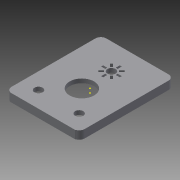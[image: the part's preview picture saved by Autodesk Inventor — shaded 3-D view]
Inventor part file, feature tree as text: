
AUTODESK INVENTOR PART (.ipt)
format: ipt  version: 2015 SP1 (Build 190203100, 203)  size: 220,160 bytes
history: native  units: mm
features: sketch x6, extrude x4, reference x4, other x2, projected_geometry x1
ambient origin geometry x8: Origin, YZ Plane, XZ Plane, XY Plane, X Axis, Y Axis, Z Axis, Center Point
bodies: Body1 (feature_tree)
feature tree (17):
  other  "Sólido1"
  sketch  "Boceto1"  dims[d0=1.5mm d1=0.0mm]
  extrude  "Extrusión1"  Depth=1.0mm
  sketch  "Boceto3"  dims[d9=9.0mm d10=1.5mm d11=0.0mm]
  other  "Labio1"
  extrude  "Extrusión2"  Depth=1.5mm TaperAngle=0.0deg
  sketch  "Boceto7"  dims[d40=1.5mm d41=80.0mm d43=360.0deg]
  extrude  "Extrusión4"  Depth=10.0mm TaperAngle=0.0deg
  extrude  "Extrusión5"  Depth=0.75mm
  sketch  "Boceto2"  dims[d2=1.0mm d3=1.0mm d4=0.0mm d5=0.0mm d6=0.0mm d7=0.0mm d8=12.5mm]
  reference  "Referencia1"
  reference  "Referencia2"
  sketch  "Boceto4"  dims[d16=10.0mm d17=0.0mm d36=10.0mm d37=0.0mm]
  reference  "Referencia3"
  reference  "Referencia4"
  sketch  "Boceto6"  dims[d38=3.0mm d39=0.75mm]
  projected_geometry  "Contorno proyectado2"
